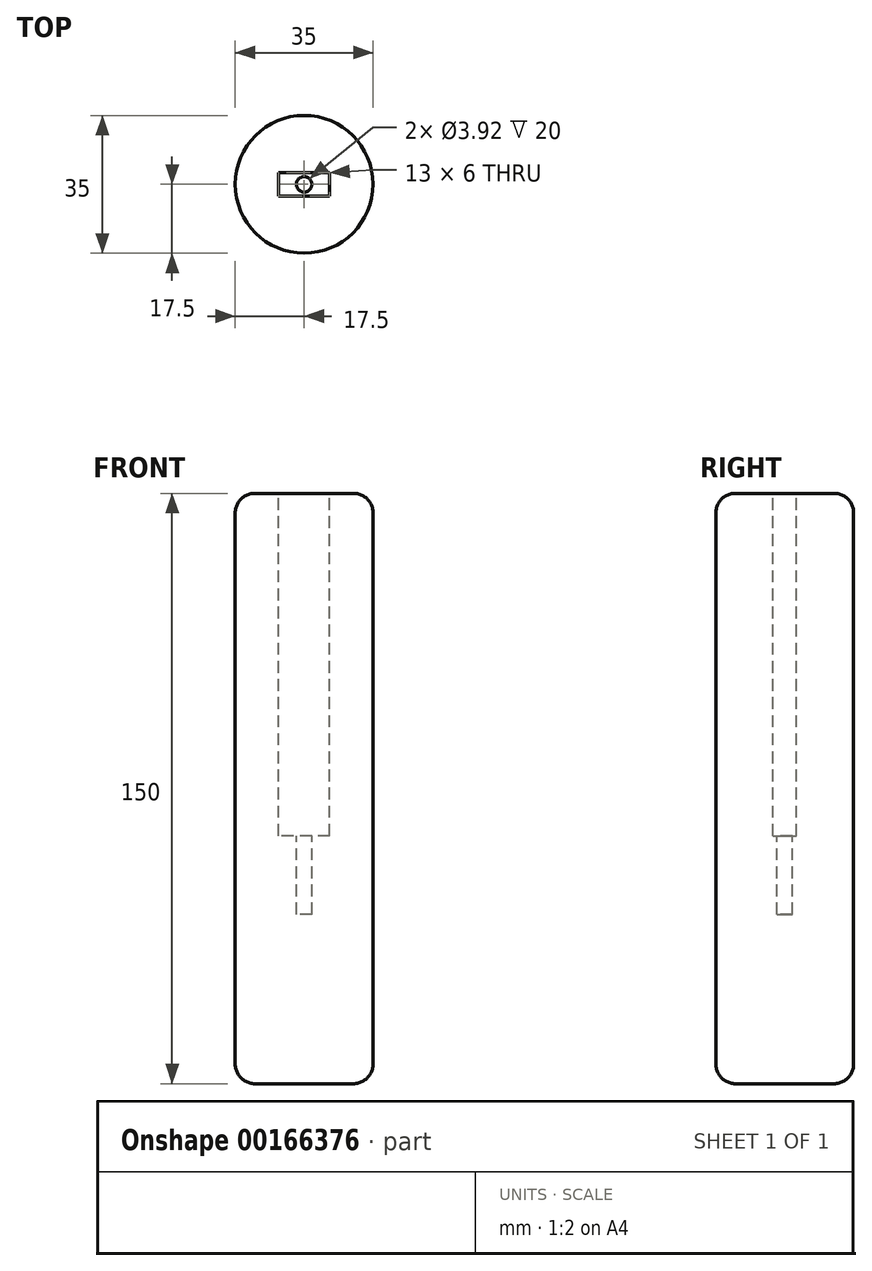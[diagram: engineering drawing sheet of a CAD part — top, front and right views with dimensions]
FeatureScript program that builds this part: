
annotation { "Feature Type Name" : "Feature", "Feature Type Description" : "" }
export const myFeature = defineFeature(function(context is Context, id is Id, definition is map)
    precondition{}
    {
        {
            var Q0;
            Q0=qCreatedBy(makeId("Top.planeOp"),FACE);
            var sketch = newSketch(context, id + "F0", { "sketchPlane" : qUnion([Q0])});
            skCircle(sketch, "E0", {"center": v(0, 0) * mm, "radius": 17.5 * mm});
            skSolve(sketch);
        }
        {
            var Q0;
            Q0 = qSketchRegion(id + "F0", true);
            extrude(context, id + "F1", {"entities" : qUnion([Q0]), "depth" : 150 * mm});
        }
        {
            var Q0;
            Q0=makeQuery(id+"F1.opExtrude","CAP_FACE",FACE,{"disambiguationData":[OSD([sQuery(id+"F0.wireOp",EDGE,"E0")])],"isStart":false});
            var sketch = newSketch(context, id + "F2", { "sketchPlane" : qUnion([Q0])});
            skLineSegment(sketch, "E1.bottom", {"start": v(6.5, -3) * mm, "end": v(-6.5, -3) * mm});
            skLineSegment(sketch, "E1.top", {"start": v(6.5, 3) * mm, "end": v(-6.5, 3) * mm});
            skLineSegment(sketch, "E1.left", {"start": v(6.5, -3) * mm, "end": v(6.5, 3) * mm});
            skLineSegment(sketch, "E1.right", {"start": v(-6.5, -3) * mm, "end": v(-6.5, 3) * mm});
            skPoint(sketch, "E1.middle", {"position": v(0, 0) * mm});
            skSolve(sketch);
        }
        {
            var Q0;
            Q0 = qSketchRegion(id + "F2", true);
            extrude(context, id + "F3", {"entities" : qUnion([Q0]), "operationType" : NewBodyOperationType.REMOVE, "oppositeDirection" : true, "depth" : 87 * mm});
        }
        {
            var Q0;
            Q0=makeQuery(id+"F3.boolean.opBoolean","COPY",FACE,{"derivedFrom":makeQuery(id+"F3.opExtrude","CAP_FACE",FACE,{"disambiguationData":[OSD([sQuery(id+"F2.wireOp",EDGE,"E1.bottom"),sQuery(id+"F2.wireOp",EDGE,"E1.top"),sQuery(id+"F2.wireOp",EDGE,"E1.left"),sQuery(id+"F2.wireOp",EDGE,"E1.right")])],"isStart":false})});
            var sketch = newSketch(context, id + "F4", { "sketchPlane" : qUnion([Q0])});
            skCircle(sketch, "E2", {"center": v(0, 0) * mm, "radius": 1.96 * mm});
            skSolve(sketch);
        }
        {
            var Q0;
            Q0 = qSketchRegion(id + "F4", true);
            extrude(context, id + "F5", {"entities" : qUnion([Q0]), "operationType" : NewBodyOperationType.REMOVE, "oppositeDirection" : true, "depth" : 20 * mm});
        }
        {
            var Q0;
            Q0=makeQuery(id+"F1.opExtrude","CAP_EDGE",EDGE,{"disambiguationData":[OSD([sQuery(id+"F0.wireOp",EDGE,"E0")])],"isStart":false});
            var Q1;
            Q1=makeQuery(id+"F1.opExtrude","CAP_EDGE",EDGE,{"disambiguationData":[OSD([sQuery(id+"F0.wireOp",EDGE,"E0")])],"isStart":true});
            fillet(context, id + "F6", {"entities" : qUnion([Q0, Q1]), "radius" : 5 * mm, "tangentPropagation" : true, "allowEdgeOverflow" : false});
        }
    });
